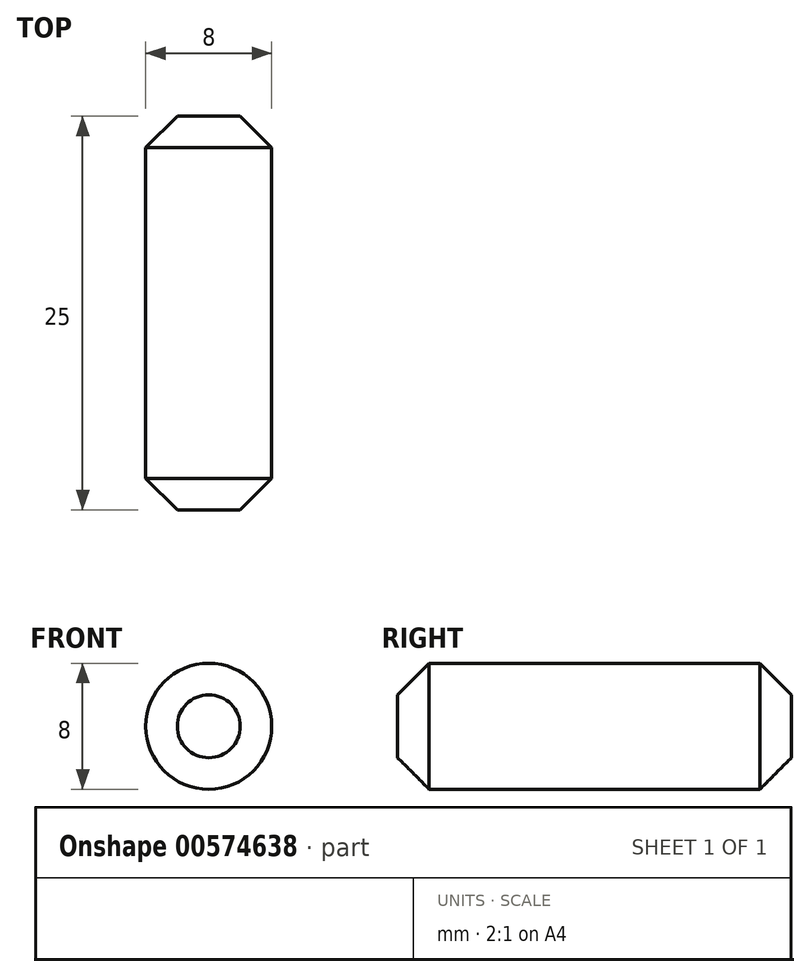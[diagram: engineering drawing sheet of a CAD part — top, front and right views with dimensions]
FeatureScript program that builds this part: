
annotation { "Feature Type Name" : "Feature", "Feature Type Description" : "" }
export const myFeature = defineFeature(function(context is Context, id is Id, definition is map)
    precondition{}
    {
        {
            var Q0;
            Q0=qCreatedBy(makeId("Front.planeOp"),FACE);
            var sketch = newSketch(context, id + "F0", { "sketchPlane" : qUnion([Q0])});
            skCircle(sketch, "E0", {"center": v(0, 0) * mm, "radius": 4 * mm});
            skSolve(sketch);
        }
        {
            var Q0;
            Q0 = qSketchRegion(id + "F0", true);
            extrude(context, id + "F1", {"entities" : qUnion([Q0]), "depth" : 25 * mm, "offsetDistance" : 25 * mm});
        }
        {
            var Q0;
            Q0=makeQuery(id+"F1.opExtrude","CAP_EDGE",EDGE,{"disambiguationData":[OSD([sQuery(id+"F0.wireOp",EDGE,"E0")])],"isStart":false});
            var Q1;
            Q1=makeQuery(id+"F1.opExtrude","CAP_EDGE",EDGE,{"disambiguationData":[OSD([sQuery(id+"F0.wireOp",EDGE,"E0")])],"isStart":true});
            chamfer(context, id + "F2", {"entities" : qUnion([Q0, Q1]), "chamferType" : ChamferType.OFFSET_ANGLE, "width" : 2 * mm, "oppositeDirection" : false, "angle" : 45 * degree, "tangentPropagation" : true});
        }
    });
